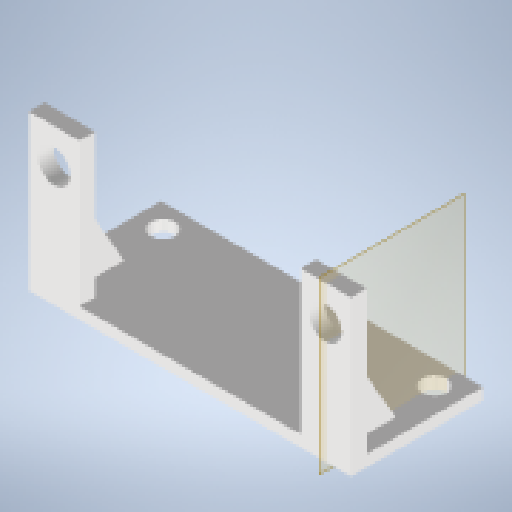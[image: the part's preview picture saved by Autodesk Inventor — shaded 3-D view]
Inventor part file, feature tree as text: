
AUTODESK INVENTOR PART (.ipt)
format: ipt  version: 2025.3 (Build 293356000, 356)  size: 175,616 bytes
history: native  units: mm
features: sketch x3, extrude x3, other x2, mirror x1, hole x1
ambient origin geometry x8: Origin, YZ Plane, XZ Plane, XY Plane, X Axis, Y Axis, Z Axis, Center Point
bodies: Body1 (feature_tree)
feature tree (10):
  other  "ソリッド1"
  sketch  "スケッチ1"
  extrude  "前"  Depth=28.0mm
  extrude  "底"  Depth=1.5mm
  other  "作業平面1"
  extrude  "リブ"  Depth=8.0mm
  mirror  "ミラー1"
  hole  "穴1"  [1 undecoded]
  sketch  "スケッチ2"
  sketch  "スケッチ3"
note: 1 required parameter value undecoded (feature->parameter linkage not recoverable at this tier; creation-order binding heuristic only, values carry confidence <= 0.55)
